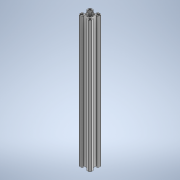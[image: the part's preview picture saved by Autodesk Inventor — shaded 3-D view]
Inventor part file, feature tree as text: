
AUTODESK INVENTOR PART (.ipt)
format: ipt  version: 2020 (Build 240168000, 168)  size: 6,824,448 bytes
history: native  units: in
note: dims shown in document units (in); Inventor stores cm internally (conversion verified against a paired STEP export)
features: extrude x1, sketch x1
ambient origin geometry x8: Origin, YZ Plane, XZ Plane, XY Plane, X Axis, Y Axis, Z Axis, Center Point
bodies: Solid1 (feature_tree)
feature tree (2):
  extrude  "Extrusion1"  Depth=3.875in TaperAngle=0.0deg
  sketch  "Sketch1"  dims[d0=0.5in d1=3.875in d2=0.0in]
